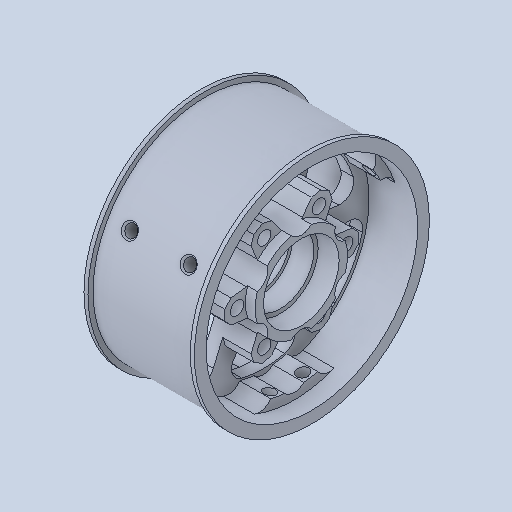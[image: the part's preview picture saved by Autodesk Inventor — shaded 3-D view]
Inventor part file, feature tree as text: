
AUTODESK INVENTOR PART (.ipt)
format: ipt  version: 2023.4 (Build 274418000, 418)  size: 356,864 bytes
history: native  units: in
note: dims shown in document units (in); Inventor stores cm internally (conversion verified against a paired STEP export)
features: mirror x1
ambient origin geometry x8: Origin, YZ Plane, XZ Plane, XY Plane, X Axis, Y Axis, Z Axis, Center Point
bodies: Solid1 (feature_tree)
feature tree (1):
  mirror  "Mirror3"
